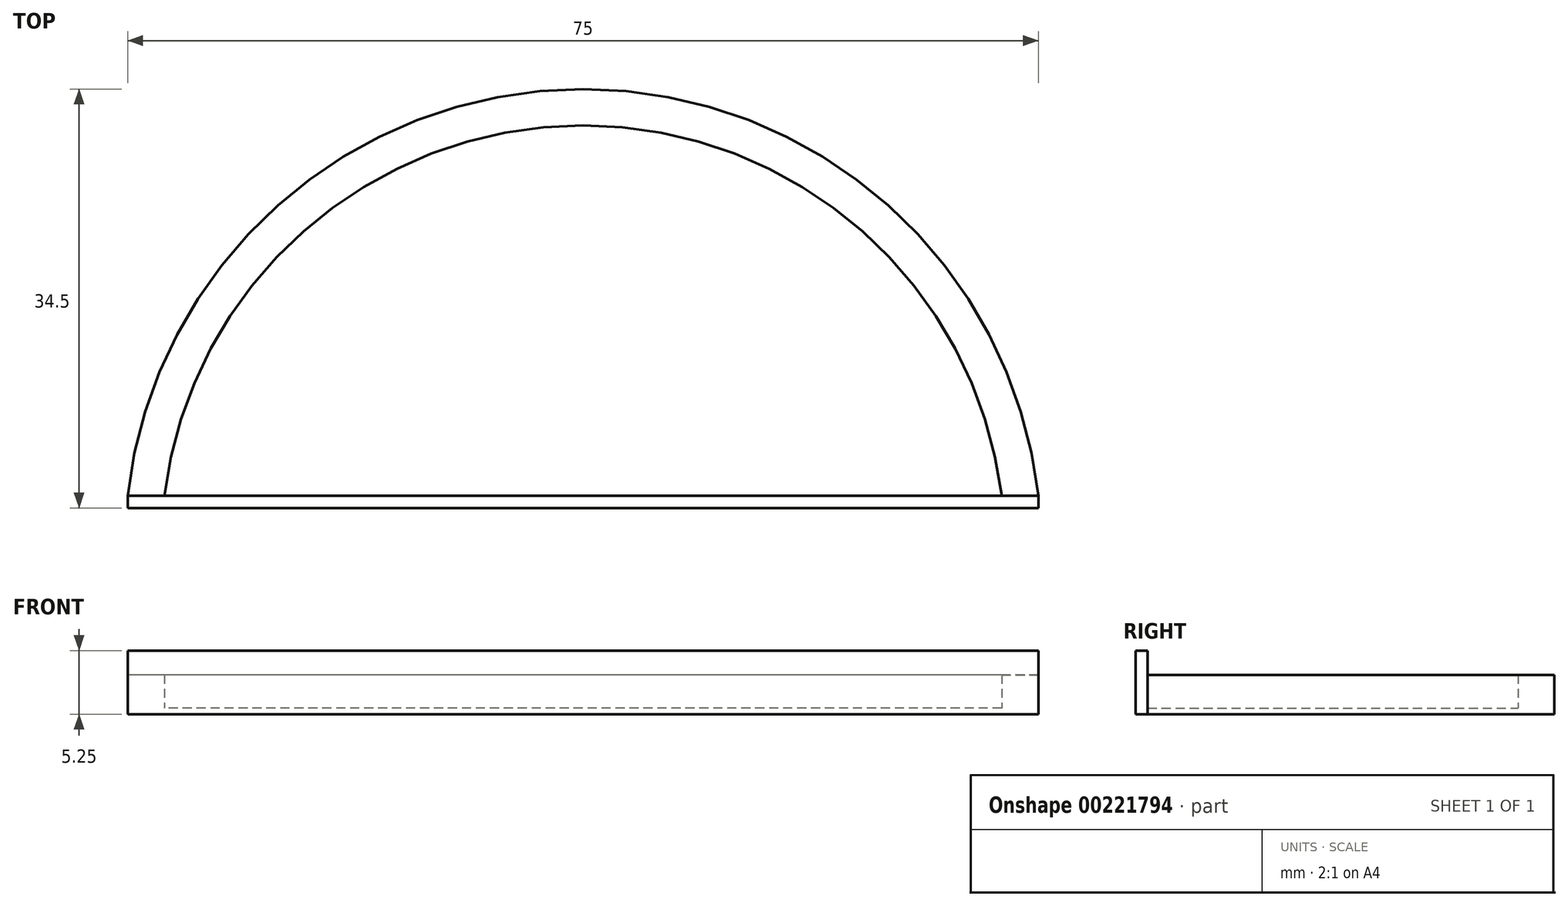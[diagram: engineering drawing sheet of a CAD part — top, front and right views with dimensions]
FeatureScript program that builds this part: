
annotation { "Feature Type Name" : "Feature", "Feature Type Description" : "" }
export const myFeature = defineFeature(function(context is Context, id is Id, definition is map)
    precondition{}
    {
        {
            var Q0;
            Q0=qCreatedBy(makeId("Top.planeOp"),FACE);
            var sketch = newSketch(context, id + "F0", { "sketchPlane" : qUnion([Q0])});
            skLineSegment(sketch, "E0", {"start": v(0, 0) * mm, "end": v(37.5, 0) * mm});
            skLineSegment(sketch, "E1", {"start": v(0, 0) * mm, "end": v(-37.5, 0) * mm});
            skPoint(sketch, "E2", {"position": v(0, 33.5) * mm});
            skArc(sketch, "E3", {"start": v(37.5, 0) * mm, "mid": v(0, 33.5) * mm, "end": v(-37.5, 0) * mm});
            skArc(sketch, "E4.0", {"start": v(34.48, 0) * mm, "mid": v(0, 30.5) * mm, "end": v(-34.48, 0) * mm});
            skLineSegment(sketch, "E5.bottom", {"start": v(-37.5, 0) * mm, "end": v(37.5, 0) * mm});
            skLineSegment(sketch, "E5.top", {"start": v(-37.5, -1) * mm, "end": v(37.5, -1) * mm});
            skLineSegment(sketch, "E5.left", {"start": v(-37.5, 0) * mm, "end": v(-37.5, -1) * mm});
            skLineSegment(sketch, "E5.right", {"start": v(37.5, 0) * mm, "end": v(37.5, -1) * mm});
            skSolve(sketch);
        }
        {
            var Q0;
            {var subQ0=sQuery(id+"F0.wireOp",EDGE,"E3");Q0=makeQuery(id+"F0.imprint","IMPRINT",FACE,{"disambiguationData":[TD([[makeQuery(id+"F0.imprint","IMPRINT",EDGE,{"derivedFrom":subQ0}),1.0]])]});}
            extrude(context, id + "F1", {"entities" : qUnion([Q0]), "depth" : 3.25 * mm});
        }
        {
            var Q0;
            {var subQ3=sQuery(id+"F0.wireOp",EDGE,"E4.0");Q0=makeQuery(id+"F0.imprint","IMPRINT",FACE,{"disambiguationData":[TD([[makeQuery(id+"F0.imprint","IMPRINT",EDGE,{"derivedFrom":subQ3}),1.0]])]});}
            extrude(context, id + "F2", {"entities" : qUnion([Q0]), "operationType" : NewBodyOperationType.ADD, "depth" : .5 * mm});
        }
        {
            var Q0;
            Q0=makeQuery(id+"F0.imprint","IMPRINT",FACE,{"disambiguationData":[TD([[makeQuery(id+"F0.imprint","IMPRINT",EDGE,{"derivedFrom":sQuery(id+"F0.wireOp",EDGE,"E5.top")}),1.0]])]});
            extrude(context, id + "F3", {"entities" : qUnion([Q0]), "operationType" : NewBodyOperationType.ADD, "depth" : 5.25 * mm});
        }
    });
